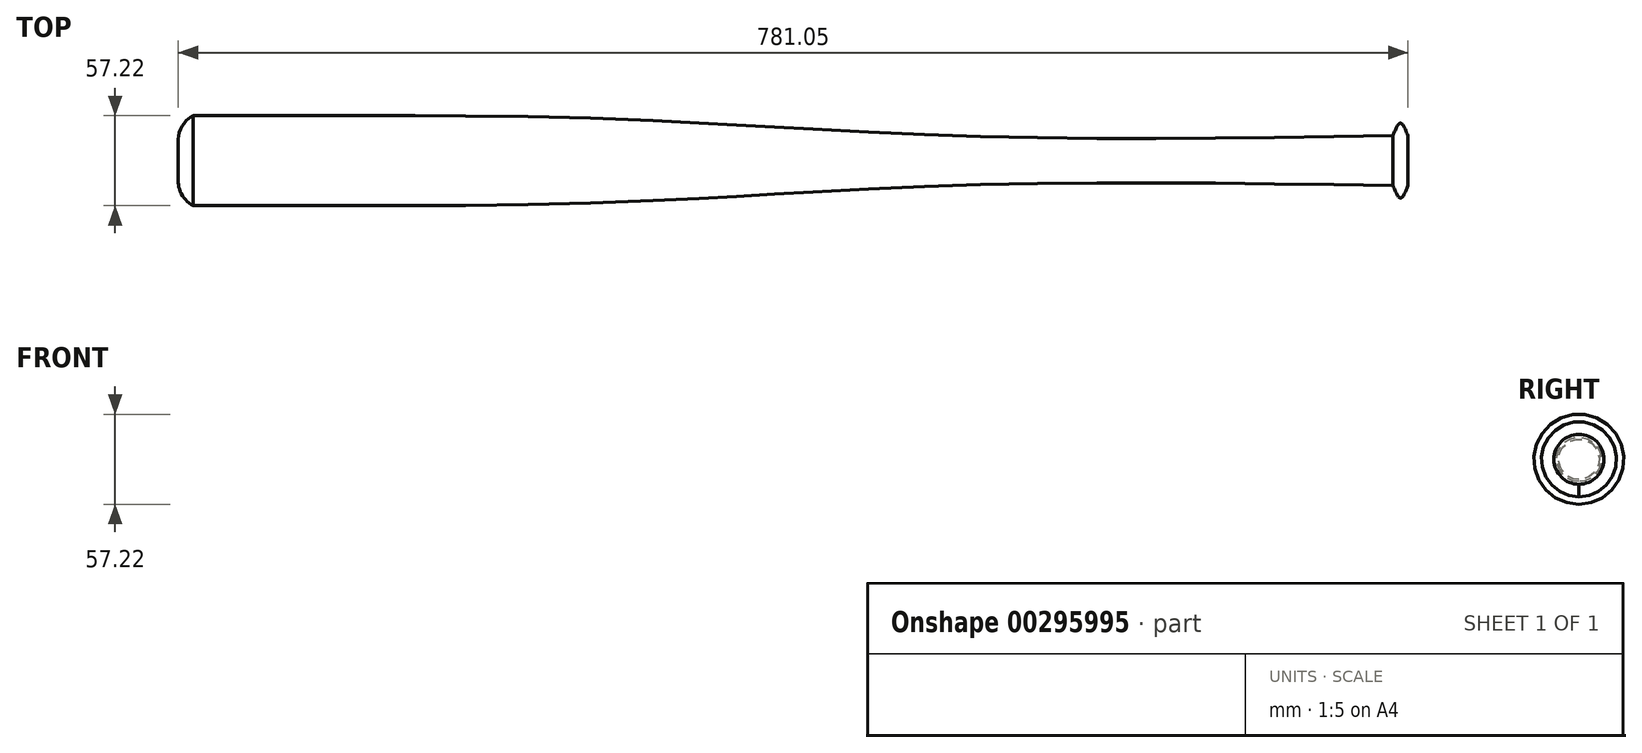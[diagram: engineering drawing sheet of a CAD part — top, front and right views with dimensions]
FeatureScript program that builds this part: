
annotation { "Feature Type Name" : "Feature", "Feature Type Description" : "" }
export const myFeature = defineFeature(function(context is Context, id is Id, definition is map)
    precondition{}
    {
        {
            var Q0;
            Q0=qCreatedBy(makeId("Right.planeOp"),FACE);
            var sketch = newSketch(context, id + "F0", { "sketchPlane" : qUnion([Q0])});
            skCircle(sketch, "E0", {"center": v(0, 0) * mm, "radius": 23.81 * mm});
            skSolve(sketch);
        }
        {
            var Q0;
            Q0=qCreatedBy(makeId("Right.planeOp"),FACE);
            cPlane(context, id + "F1", {"entities" : qUnion([Q0]), "cplaneType" : CPlaneType.OFFSET, "offset" : 9.52 * mm, "width" : 152.4 * mm, "height" : 152.4 * mm});
        }
        {
            var Q0;
            Q0=qCreatedBy(id+"F1.planeOp",FACE);
            var sketch = newSketch(context, id + "F2", { "sketchPlane" : qUnion([Q0])});
            skCircle(sketch, "E1", {"center": v(0, 0) * mm, "radius": 28.58 * mm});
            skSolve(sketch);
        }
        {
            var Q0;
            Q0=qCreatedBy(id+"F1.planeOp",FACE);
            cPlane(context, id + "F3", {"entities" : qUnion([Q0]), "cplaneType" : CPlaneType.OFFSET, "offset" : 127 * mm, "width" : 152.4 * mm, "height" : 152.4 * mm});
        }
        {
            var Q0;
            Q0=qCreatedBy(id+"F3.planeOp",FACE);
            var sketch = newSketch(context, id + "F4", { "sketchPlane" : qUnion([Q0])});
            skCircle(sketch, "E2", {"center": v(0, 0) * mm, "radius": 28.57 * mm});
            skSolve(sketch);
        }
        {
            var Q0;
            Q0=qCreatedBy(id+"F3.planeOp",FACE);
            cPlane(context, id + "F5", {"entities" : qUnion([Q0]), "cplaneType" : CPlaneType.OFFSET, "offset" : 127 * mm, "width" : 152.4 * mm, "height" : 152.4 * mm});
        }
        {
            var Q0;
            Q0=qCreatedBy(id+"F5.planeOp",FACE);
            var sketch = newSketch(context, id + "F6", { "sketchPlane" : qUnion([Q0])});
            skCircle(sketch, "E3", {"center": v(0, 0) * mm, "radius": 26.99 * mm});
            skSolve(sketch);
        }
        {
            var Q0;
            Q0=qCreatedBy(id+"F5.planeOp",FACE);
            cPlane(context, id + "F7", {"entities" : qUnion([Q0]), "cplaneType" : CPlaneType.OFFSET, "offset" : 127 * mm, "width" : 152.4 * mm, "height" : 152.4 * mm});
        }
        {
            var Q0;
            Q0=qCreatedBy(id+"F7.planeOp",FACE);
            var sketch = newSketch(context, id + "F8", { "sketchPlane" : qUnion([Q0])});
            skCircle(sketch, "E4", {"center": v(0, 0) * mm, "radius": 20.64 * mm});
            skSolve(sketch);
        }
        {
            var Q0;
            Q0=qCreatedBy(id+"F7.planeOp",FACE);
            cPlane(context, id + "F9", {"entities" : qUnion([Q0]), "cplaneType" : CPlaneType.OFFSET, "offset" : 127 * mm, "width" : 152.4 * mm, "height" : 152.4 * mm});
        }
        {
            var Q0;
            Q0=qCreatedBy(id+"F9.planeOp",FACE);
            var sketch = newSketch(context, id + "F10", { "sketchPlane" : qUnion([Q0])});
            skCircle(sketch, "E5", {"center": v(0, 0) * mm, "radius": 15.08 * mm});
            skSolve(sketch);
        }
        {
            var Q0;
            Q0=qCreatedBy(id+"F9.planeOp",FACE);
            cPlane(context, id + "F11", {"entities" : qUnion([Q0]), "cplaneType" : CPlaneType.OFFSET, "offset" : 127 * mm, "width" : 152.4 * mm, "height" : 152.4 * mm});
        }
        {
            var Q0;
            Q0=qCreatedBy(id+"F11.planeOp",FACE);
            var sketch = newSketch(context, id + "F12", { "sketchPlane" : qUnion([Q0])});
            skCircle(sketch, "E6", {"center": v(0, 0) * mm, "radius": 14.29 * mm});
            skSolve(sketch);
        }
        {
            var Q0;
            Q0=qCreatedBy(id+"F11.planeOp",FACE);
            cPlane(context, id + "F13", {"entities" : qUnion([Q0]), "cplaneType" : CPlaneType.OFFSET, "offset" : 127 * mm, "width" : 152.4 * mm, "height" : 152.4 * mm});
        }
        {
            var Q0;
            Q0=qCreatedBy(id+"F13.planeOp",FACE);
            var sketch = newSketch(context, id + "F14", { "sketchPlane" : qUnion([Q0])});
            skCircle(sketch, "E7", {"center": v(0, 0) * mm, "radius": 15.88 * mm});
            skSolve(sketch);
        }
        {
            var Q0;
            Q0=qCreatedBy(id+"F13.planeOp",FACE);
            cPlane(context, id + "F15", {"entities" : qUnion([Q0]), "cplaneType" : CPlaneType.OFFSET, "offset" : 4.76 * mm, "width" : 152.4 * mm, "height" : 152.4 * mm});
        }
        {
            var Q0;
            Q0=qCreatedBy(id+"F15.planeOp",FACE);
            var sketch = newSketch(context, id + "F16", { "sketchPlane" : qUnion([Q0])});
            skCircle(sketch, "E8", {"center": v(0, 0) * mm, "radius": 23.81 * mm});
            skSolve(sketch);
        }
        {
            var Q0;
            Q0=qCreatedBy(id+"F15.planeOp",FACE);
            cPlane(context, id + "F17", {"entities" : qUnion([Q0]), "cplaneType" : CPlaneType.OFFSET, "offset" : 4.76 * mm, "width" : 152.4 * mm, "height" : 152.4 * mm});
        }
        {
            var Q0;
            Q0=qCreatedBy(id+"F17.planeOp",FACE);
            var sketch = newSketch(context, id + "F18", { "sketchPlane" : qUnion([Q0])});
            skCircle(sketch, "E9", {"center": v(0, 0) * mm, "radius": 15.88 * mm});
            skSolve(sketch);
        }
        {
            var Q0;
            Q0=makeQuery(id+"F2.imprint","IMPRINT",FACE,{"disambiguationData":[TD([[makeQuery(id+"F2.imprint","IMPRINT",EDGE,{"derivedFrom":sQuery(id+"F2.wireOp",EDGE,"E1")}),1.0]])]});
            var Q1;
            Q1=makeQuery(id+"F4.imprint","IMPRINT",FACE,{"disambiguationData":[TD([[makeQuery(id+"F4.imprint","IMPRINT",EDGE,{"derivedFrom":sQuery(id+"F4.wireOp",EDGE,"E2")}),1.0]])]});
            var Q2;
            Q2=makeQuery(id+"F6.imprint","IMPRINT",FACE,{"disambiguationData":[TD([[makeQuery(id+"F6.imprint","IMPRINT",EDGE,{"derivedFrom":sQuery(id+"F6.wireOp",EDGE,"E3")}),1.0]])]});
            var Q3;
            Q3=makeQuery(id+"F8.imprint","IMPRINT",FACE,{"disambiguationData":[TD([[makeQuery(id+"F8.imprint","IMPRINT",EDGE,{"derivedFrom":sQuery(id+"F8.wireOp",EDGE,"E4")}),1.0]])]});
            var Q4;
            Q4=makeQuery(id+"F10.imprint","IMPRINT",FACE,{"disambiguationData":[TD([[makeQuery(id+"F10.imprint","IMPRINT",EDGE,{"derivedFrom":sQuery(id+"F10.wireOp",EDGE,"E5")}),1.0]])]});
            var Q5;
            Q5=makeQuery(id+"F12.imprint","IMPRINT",FACE,{"disambiguationData":[TD([[makeQuery(id+"F12.imprint","IMPRINT",EDGE,{"derivedFrom":sQuery(id+"F12.wireOp",EDGE,"E6")}),1.0]])]});
            var Q6;
            Q6=makeQuery(id+"F14.imprint","IMPRINT",FACE,{"disambiguationData":[TD([[makeQuery(id+"F14.imprint","IMPRINT",EDGE,{"derivedFrom":sQuery(id+"F14.wireOp",EDGE,"E7")}),1.0]])]});
            loft(context, id + "F19", {"sheetProfilesArray" : [{ "sheetProfileEntities" : qUnion([Q0]) }, { "sheetProfileEntities" : qUnion([Q1]) }, { "sheetProfileEntities" : qUnion([Q2]) }, { "sheetProfileEntities" : qUnion([Q3]) }, { "sheetProfileEntities" : qUnion([Q4]) }, { "sheetProfileEntities" : qUnion([Q5]) }, { "sheetProfileEntities" : qUnion([Q6]) }]});
        }
        {
            var Q0;
            Q0=makeQuery(id+"F14.imprint","IMPRINT",FACE,{"disambiguationData":[TD([[makeQuery(id+"F14.imprint","IMPRINT",EDGE,{"derivedFrom":sQuery(id+"F14.wireOp",EDGE,"E7")}),1.0]])]});
            var Q1;
            Q1=makeQuery(id+"F16.imprint","IMPRINT",FACE,{"disambiguationData":[TD([[makeQuery(id+"F16.imprint","IMPRINT",EDGE,{"derivedFrom":sQuery(id+"F16.wireOp",EDGE,"E8")}),1.0]])]});
            var Q2;
            Q2=makeQuery(id+"F18.imprint","IMPRINT",FACE,{"disambiguationData":[TD([[makeQuery(id+"F18.imprint","IMPRINT",EDGE,{"derivedFrom":sQuery(id+"F18.wireOp",EDGE,"E9")}),1.0]])]});
            loft(context, id + "F20", {"operationType" : NewBodyOperationType.ADD, "sheetProfilesArray" : [{ "sheetProfileEntities" : qUnion([Q0]) }, { "sheetProfileEntities" : qUnion([Q1]) }, { "sheetProfileEntities" : qUnion([Q2]) }]});
        }
        {
            var Q0;
            Q0=makeQuery(id+"F0.imprint","IMPRINT",FACE,{"disambiguationData":[TD([[makeQuery(id+"F0.imprint","IMPRINT",EDGE,{"derivedFrom":sQuery(id+"F0.wireOp",EDGE,"E0")}),1.0]])]});
            var Q1;
            Q1=makeQuery(id+"F2.imprint","IMPRINT",FACE,{"disambiguationData":[TD([[makeQuery(id+"F2.imprint","IMPRINT",EDGE,{"derivedFrom":sQuery(id+"F2.wireOp",EDGE,"E1")}),1.0]])]});
            loft(context, id + "F21", {"operationType" : NewBodyOperationType.ADD, "sheetProfilesArray" : [{ "sheetProfileEntities" : qUnion([Q0]) }, { "sheetProfileEntities" : qUnion([Q1]) }]});
        }
        {
            var Q0;
            Q0=makeQuery(id+"F21.opLoft","MID_CAP_EDGE",EDGE,{"disambiguationData":[OSD([sQuery(id+"F0.wireOp",EDGE,"E0")])],"capPos":0.0});
            fillet(context, id + "F22", {"entities" : qUnion([Q0]), "radius" : 17.78 * mm, "tangentPropagation" : true, "allowEdgeOverflow" : false});
        }
    });
